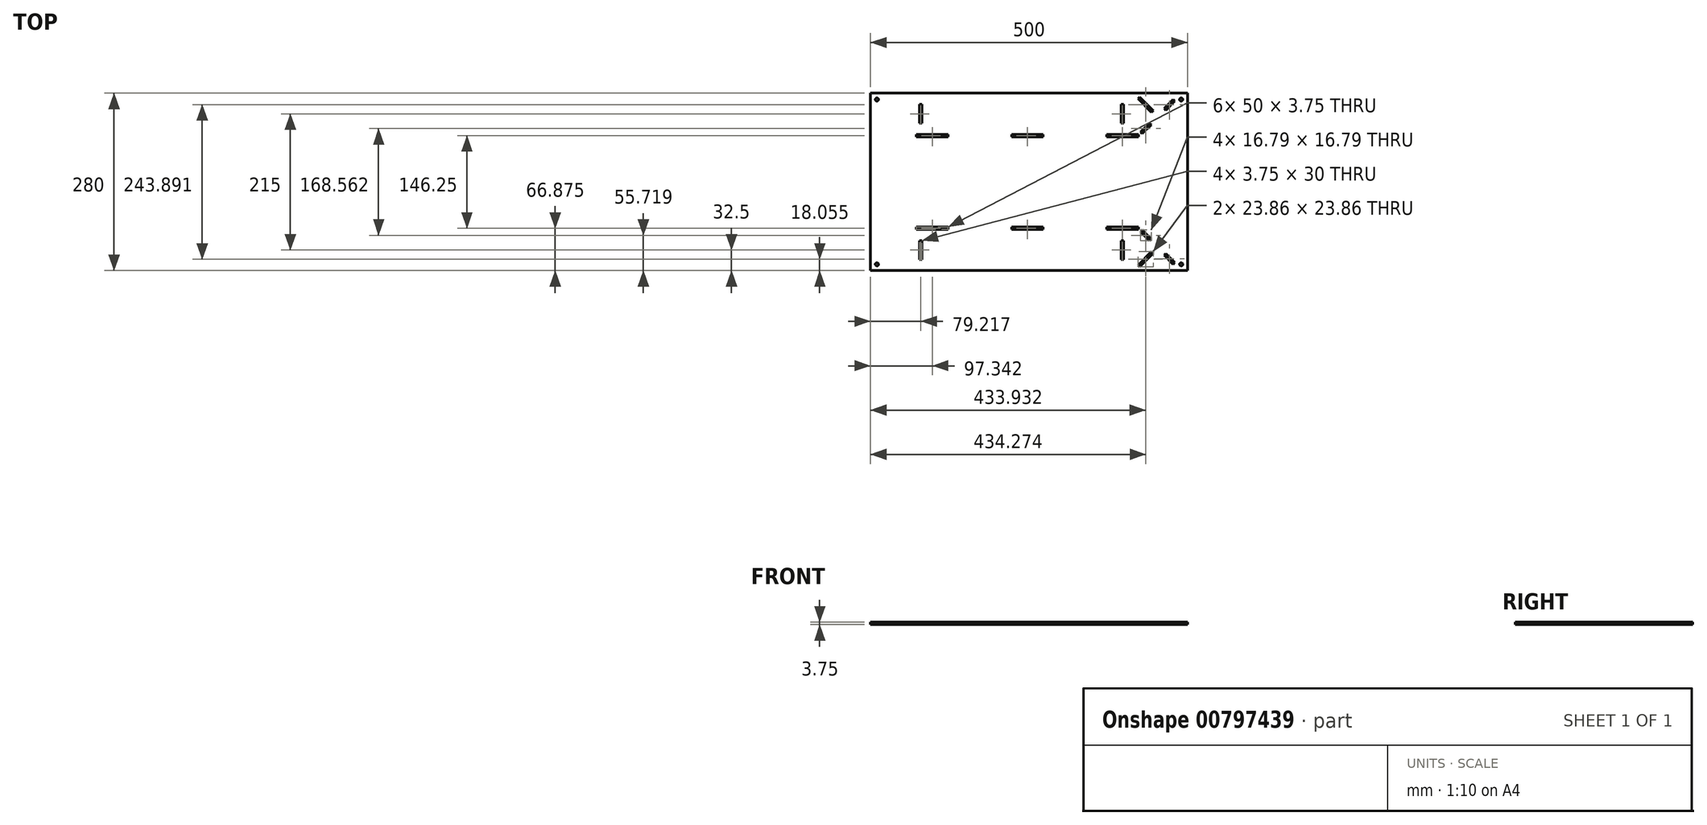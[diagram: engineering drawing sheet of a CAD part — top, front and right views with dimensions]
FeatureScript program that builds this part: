
annotation { "Feature Type Name" : "Feature", "Feature Type Description" : "" }
export const myFeature = defineFeature(function(context is Context, id is Id, definition is map)
    precondition{}
    {
        {
            var Q0;
            Q0=qCreatedBy(makeId("Top.planeOp"),FACE);
            var sketch = newSketch(context, id + "F0", { "sketchPlane" : qUnion([Q0])});
            skLineSegment(sketch, "E0.bottom", {"start": v(12.1, 0) * mm, "end": v(462.1, 0) * mm});
            skLineSegment(sketch, "E0.top", {"start": v(62.1, 280) * mm, "end": v(462.1, 280) * mm});
            skLineSegment(sketch, "E0.right", {"start": v(462.1, 0) * mm, "end": v(462.1, 280) * mm});
            skLineSegment(sketch, "E1.bottom", {"start": v(184.43, 215) * mm, "end": v(234.43, 215) * mm});
            skLineSegment(sketch, "E1.top", {"start": v(184.43, 211.25) * mm, "end": v(234.43, 211.25) * mm});
            skLineSegment(sketch, "E1.left", {"start": v(184.43, 215) * mm, "end": v(184.43, 211.25) * mm});
            skLineSegment(sketch, "E1.right", {"start": v(234.43, 215) * mm, "end": v(234.43, 211.25) * mm});
            skLineSegment(sketch, "E2.MirrorCS", {"start": v(334.43, 215) * mm, "end": v(334.43, 215) * mm});
            skLineSegment(sketch, "E3.MirrorCS", {"start": v(134.43, 65) * mm, "end": v(234.43, 65) * mm});
            skLineSegment(sketch, "E4.MirrorCS", {"start": v(334.43, 65) * mm, "end": v(334.43, 65) * mm});
            skLineSegment(sketch, "E5.bottom", {"start": v(357.56, 262.5) * mm, "end": v(361.3, 262.5) * mm});
            skLineSegment(sketch, "E5.top", {"start": v(357.56, 232.5) * mm, "end": v(361.3, 232.5) * mm});
            skLineSegment(sketch, "E5.left", {"start": v(357.56, 262.5) * mm, "end": v(357.56, 232.5) * mm});
            skLineSegment(sketch, "E5.right", {"start": v(361.3, 262.5) * mm, "end": v(361.3, 232.5) * mm});
            skLineSegment(sketch, "E6.bottom", {"start": v(334.43, 215) * mm, "end": v(384.43, 215) * mm});
            skLineSegment(sketch, "E6.top", {"start": v(334.43, 211.25) * mm, "end": v(384.43, 211.25) * mm});
            skLineSegment(sketch, "E6.left", {"start": v(334.43, 215) * mm, "end": v(334.43, 211.25) * mm});
            skLineSegment(sketch, "E6.right", {"start": v(384.43, 215) * mm, "end": v(384.43, 211.25) * mm});
            skLineSegment(sketch, "E7.bottom", {"start": v(234.43, 65) * mm, "end": v(184.43, 65) * mm});
            skLineSegment(sketch, "E7.top", {"start": v(234.43, 68.75) * mm, "end": v(184.43, 68.75) * mm});
            skLineSegment(sketch, "E7.left", {"start": v(234.43, 65) * mm, "end": v(234.43, 68.75) * mm});
            skLineSegment(sketch, "E7.right", {"start": v(184.43, 65) * mm, "end": v(184.43, 68.75) * mm});
            skLineSegment(sketch, "E8.bottom", {"start": v(334.43, 65) * mm, "end": v(384.43, 65) * mm});
            skLineSegment(sketch, "E8.top", {"start": v(334.43, 68.75) * mm, "end": v(384.43, 68.75) * mm});
            skLineSegment(sketch, "E8.left", {"start": v(334.43, 65) * mm, "end": v(334.43, 68.75) * mm});
            skLineSegment(sketch, "E8.right", {"start": v(384.43, 65) * mm, "end": v(384.43, 68.75) * mm});
            skLineSegment(sketch, "E9.bottom", {"start": v(357.56, 47.5) * mm, "end": v(361.3, 47.5) * mm});
            skLineSegment(sketch, "E9.top", {"start": v(357.56, 17.5) * mm, "end": v(361.3, 17.5) * mm});
            skLineSegment(sketch, "E9.left", {"start": v(357.56, 47.5) * mm, "end": v(357.56, 17.5) * mm});
            skLineSegment(sketch, "E9.right", {"start": v(361.3, 47.5) * mm, "end": v(361.3, 17.5) * mm});
            skLineSegment(sketch, "E10.bottom", {"start": v(62.1, 280) * mm, "end": v(-37.9, 280) * mm});
            skLineSegment(sketch, "E10.top", {"start": v(12.1, 0) * mm, "end": v(-37.9, 0) * mm});
            skLineSegment(sketch, "E10.right", {"start": v(-37.9, 280) * mm, "end": v(-37.9, 0) * mm});
            skLineSegment(sketch, "E11.bottom", {"start": v(84.43, 215) * mm, "end": v(34.43, 215) * mm});
            skLineSegment(sketch, "E11.top", {"start": v(84.43, 211.25) * mm, "end": v(34.43, 211.25) * mm});
            skLineSegment(sketch, "E11.left", {"start": v(84.43, 215) * mm, "end": v(84.43, 211.25) * mm});
            skLineSegment(sketch, "E11.right", {"start": v(34.43, 215) * mm, "end": v(34.43, 211.25) * mm});
            skLineSegment(sketch, "E12.bottom", {"start": v(84.43, 68.75) * mm, "end": v(34.43, 68.75) * mm});
            skLineSegment(sketch, "E12.top", {"start": v(84.43, 65) * mm, "end": v(34.43, 65) * mm});
            skLineSegment(sketch, "E12.left", {"start": v(84.43, 68.75) * mm, "end": v(84.43, 65) * mm});
            skLineSegment(sketch, "E12.right", {"start": v(34.43, 68.75) * mm, "end": v(34.43, 65) * mm});
            skLineSegment(sketch, "E13.bottom", {"start": v(39.43, 262.5) * mm, "end": v(43.18, 262.5) * mm});
            skLineSegment(sketch, "E13.top", {"start": v(39.43, 232.5) * mm, "end": v(43.18, 232.5) * mm});
            skLineSegment(sketch, "E13.left", {"start": v(39.43, 262.5) * mm, "end": v(39.43, 232.5) * mm});
            skLineSegment(sketch, "E13.right", {"start": v(43.18, 262.5) * mm, "end": v(43.18, 232.5) * mm});
            skLineSegment(sketch, "E14.bottom", {"start": v(39.43, 47.5) * mm, "end": v(43.18, 47.5) * mm});
            skLineSegment(sketch, "E14.top", {"start": v(39.43, 17.5) * mm, "end": v(43.18, 17.5) * mm});
            skLineSegment(sketch, "E14.left", {"start": v(39.43, 47.5) * mm, "end": v(39.43, 17.5) * mm});
            skLineSegment(sketch, "E14.right", {"start": v(43.18, 47.5) * mm, "end": v(43.18, 17.5) * mm});
            skSolve(sketch);
        }
        {
            var Q0;
            Q0=makeQuery(id+"F0.imprint","IMPRINT",FACE,{"disambiguationData":[TD([[makeQuery(id+"F0.imprint","IMPRINT",EDGE,{"derivedFrom":sQuery(id+"F0.wireOp",EDGE,"E0.bottom")}),1.0]])]});
            extrude(context, id + "F1", {"entities" : qUnion([Q0]), "depth" : 3.75 * mm, "offsetDistance" : 25 * mm});
        }
        {
            var Q0;
            Q0=makeQuery(id+"F1.opExtrude","CAP_FACE",FACE,{"disambiguationData":[OSD([sQuery(id+"F0.wireOp",EDGE,"E0.bottom"),sQuery(id+"F0.wireOp",EDGE,"E0.top"),sQuery(id+"F0.wireOp",EDGE,"E0.left"),sQuery(id+"F0.wireOp",EDGE,"E0.right"),sQuery(id+"F0.wireOp",EDGE,"E1.bottom"),sQuery(id+"F0.wireOp",EDGE,"E1.top"),sQuery(id+"F0.wireOp",EDGE,"E1.left"),sQuery(id+"F0.wireOp",EDGE,"E1.right"),sQuery(id+"F0.wireOp",EDGE,"e73540e0-437e-4d11-b89e-325f1f7d4c790.MirrorCS"),sQuery(id+"F0.wireOp",EDGE,"E2.MirrorCS"),sQuery(id+"F0.wireOp",EDGE,"06532218-7f8b-4a41-8e3c-2a9fed56a3b10.MirrorCS"),sQuery(id+"F0.wireOp",EDGE,"7cb798fc-15e8-495b-8a35-73028b4edfa90.MirrorCS"),sQuery(id+"F0.wireOp",EDGE,"545d7cc9-1fc7-4841-af53-376eaec099370.MirrorCS"),sQuery(id+"F0.wireOp",EDGE,"E3.MirrorCS"),sQuery(id+"F0.wireOp",EDGE,"9b8ca559-61c4-4ae6-86d6-e5e959e65d2c0.MirrorCS"),sQuery(id+"F0.wireOp",EDGE,"461afd8d-256b-4b3b-8858-7b4be28ac2ee0.MirrorCS"),sQuery(id+"F0.wireOp",EDGE,"ccdc6204-bf97-4cc3-8a27-938706aa7f700.MirrorCS"),sQuery(id+"F0.wireOp",EDGE,"E4.MirrorCS"),sQuery(id+"F0.wireOp",EDGE,"de380e3f-fddb-4eb0-9c14-f8c98a16e2c70.MirrorCS"),sQuery(id+"F0.wireOp",EDGE,"ee423979-f3e1-44e8-98c6-b9dc3032ede40.MirrorCS"),sQuery(id+"F0.wireOp",EDGE,"E5.bottom"),sQuery(id+"F0.wireOp",EDGE,"E5.top"),sQuery(id+"F0.wireOp",EDGE,"E5.left"),sQuery(id+"F0.wireOp",EDGE,"E5.right"),sQuery(id+"F0.wireOp",EDGE,"2a4d6bfd-6cea-46ef-a5a2-565ee4e24cbc0.MirrorCS"),sQuery(id+"F0.wireOp",EDGE,"e7e3dcee-2f9a-4279-8a5c-00eaed48cf630.MirrorCS"),sQuery(id+"F0.wireOp",EDGE,"b1a6a120-30f8-47bb-a578-e070e3f1ff540.MirrorCS"),sQuery(id+"F0.wireOp",EDGE,"80d5920c-4993-49ba-a786-e7242780b6720.MirrorCS")])],"isStart":false});
            var sketch = newSketch(context, id + "F2", { "sketchPlane" : qUnion([Q0])});
            skPoint(sketch, "E15", {"position": v(-27.9, 10) * mm});
            skPoint(sketch, "E16", {"position": v(-27.9, 270) * mm});
            skPoint(sketch, "E17", {"position": v(452.1, 270) * mm});
            skPoint(sketch, "E18", {"position": v(452.1, 10) * mm});
            skSolve(sketch);
        }
        {
            var Q0;
            Q0=sQuery(id+"F2.wireOp",VERTEX,"E15");
            var Q1;
            Q1=sQuery(id+"F2.wireOp",VERTEX,"E16");
            var Q2;
            Q2=sQuery(id+"F2.wireOp",VERTEX,"E18");
            var Q3;
            Q3=sQuery(id+"F2.wireOp",VERTEX,"E17");
            var Q4;
            Q4=makeQuery(id+"F1.opExtrude","SWEPT_BODY",BODY,{"disambiguationData":[OSD([sQuery(id+"F0.wireOp",EDGE,"E0.bottom"),sQuery(id+"F0.wireOp",EDGE,"E0.top"),sQuery(id+"F0.wireOp",EDGE,"E0.left"),sQuery(id+"F0.wireOp",EDGE,"E0.right"),sQuery(id+"F0.wireOp",EDGE,"E1.bottom"),sQuery(id+"F0.wireOp",EDGE,"E1.top"),sQuery(id+"F0.wireOp",EDGE,"E1.left"),sQuery(id+"F0.wireOp",EDGE,"E1.right"),sQuery(id+"F0.wireOp",EDGE,"e73540e0-437e-4d11-b89e-325f1f7d4c790.MirrorCS"),sQuery(id+"F0.wireOp",EDGE,"E2.MirrorCS"),sQuery(id+"F0.wireOp",EDGE,"06532218-7f8b-4a41-8e3c-2a9fed56a3b10.MirrorCS"),sQuery(id+"F0.wireOp",EDGE,"7cb798fc-15e8-495b-8a35-73028b4edfa90.MirrorCS"),sQuery(id+"F0.wireOp",EDGE,"545d7cc9-1fc7-4841-af53-376eaec099370.MirrorCS"),sQuery(id+"F0.wireOp",EDGE,"E3.MirrorCS"),sQuery(id+"F0.wireOp",EDGE,"9b8ca559-61c4-4ae6-86d6-e5e959e65d2c0.MirrorCS"),sQuery(id+"F0.wireOp",EDGE,"461afd8d-256b-4b3b-8858-7b4be28ac2ee0.MirrorCS"),sQuery(id+"F0.wireOp",EDGE,"ccdc6204-bf97-4cc3-8a27-938706aa7f700.MirrorCS"),sQuery(id+"F0.wireOp",EDGE,"E4.MirrorCS"),sQuery(id+"F0.wireOp",EDGE,"de380e3f-fddb-4eb0-9c14-f8c98a16e2c70.MirrorCS"),sQuery(id+"F0.wireOp",EDGE,"ee423979-f3e1-44e8-98c6-b9dc3032ede40.MirrorCS"),sQuery(id+"F0.wireOp",EDGE,"E5.bottom"),sQuery(id+"F0.wireOp",EDGE,"E5.top"),sQuery(id+"F0.wireOp",EDGE,"E5.left"),sQuery(id+"F0.wireOp",EDGE,"E5.right"),sQuery(id+"F0.wireOp",EDGE,"2a4d6bfd-6cea-46ef-a5a2-565ee4e24cbc0.MirrorCS"),sQuery(id+"F0.wireOp",EDGE,"e7e3dcee-2f9a-4279-8a5c-00eaed48cf630.MirrorCS"),sQuery(id+"F0.wireOp",EDGE,"b1a6a120-30f8-47bb-a578-e070e3f1ff540.MirrorCS"),sQuery(id+"F0.wireOp",EDGE,"80d5920c-4993-49ba-a786-e7242780b6720.MirrorCS")])]});
            hole(context, id + "F3", {"style" : HoleStyle.SIMPLE, "endStyle" : HoleEndStyle.THROUGH, "holeDiameter" : 5 * mm, "majorDiameter" : 5 * mm, "isTappedThrough" : true, "tappedDepth" : 12 * mm, "tapClearance" : 3, "locations" : qUnion([Q0, Q1, Q2, Q3]), "scope" : qUnion([Q4])});
        }
        {
            var Q0;
            Q0=makeQuery(id+"F1.opExtrude","CAP_FACE",FACE,{"disambiguationData":[OSD([sQuery(id+"F0.wireOp",EDGE,"E0.bottom"),sQuery(id+"F0.wireOp",EDGE,"E0.top"),sQuery(id+"F0.wireOp",EDGE,"E0.left"),sQuery(id+"F0.wireOp",EDGE,"E0.right"),sQuery(id+"F0.wireOp",EDGE,"E1.bottom"),sQuery(id+"F0.wireOp",EDGE,"E1.top"),sQuery(id+"F0.wireOp",EDGE,"E1.left"),sQuery(id+"F0.wireOp",EDGE,"E1.right"),sQuery(id+"F0.wireOp",EDGE,"E5.bottom"),sQuery(id+"F0.wireOp",EDGE,"E5.top"),sQuery(id+"F0.wireOp",EDGE,"E5.left"),sQuery(id+"F0.wireOp",EDGE,"E5.right"),sQuery(id+"F0.wireOp",EDGE,"E6.bottom"),sQuery(id+"F0.wireOp",EDGE,"E6.top"),sQuery(id+"F0.wireOp",EDGE,"E6.left"),sQuery(id+"F0.wireOp",EDGE,"E6.right"),sQuery(id+"F0.wireOp",EDGE,"E7.bottom"),sQuery(id+"F0.wireOp",EDGE,"E7.top"),sQuery(id+"F0.wireOp",EDGE,"E7.left"),sQuery(id+"F0.wireOp",EDGE,"E7.right"),sQuery(id+"F0.wireOp",EDGE,"E8.bottom"),sQuery(id+"F0.wireOp",EDGE,"E8.top"),sQuery(id+"F0.wireOp",EDGE,"E8.left"),sQuery(id+"F0.wireOp",EDGE,"E8.right"),sQuery(id+"F0.wireOp",EDGE,"E9.bottom"),sQuery(id+"F0.wireOp",EDGE,"E9.top"),sQuery(id+"F0.wireOp",EDGE,"E9.left"),sQuery(id+"F0.wireOp",EDGE,"E9.right")])],"isStart":false});
            var sketch = newSketch(context, id + "F4", { "sketchPlane" : qUnion([Q0])});
            skLineSegment(sketch, "E19", {"start": v(384.43, 215) * mm, "end": v(402.1, 232.68) * mm});
            skLineSegment(sketch, "E20", {"start": v(439.43, 270) * mm, "end": v(442.08, 267.35) * mm});
            skLineSegment(sketch, "E21", {"start": v(442.08, 267.35) * mm, "end": v(427.94, 253.2) * mm});
            skLineSegment(sketch, "E22", {"start": v(390.62, 215.88) * mm, "end": v(387.97, 218.54) * mm});
            skLineSegment(sketch, "E23", {"start": v(402.1, 232.68) * mm, "end": v(404.76, 230.03) * mm});
            skLineSegment(sketch, "E24", {"start": v(425.29, 255.86) * mm, "end": v(427.94, 253.2) * mm});
            skLineSegment(sketch, "E25.trimOffspring", {"start": v(425.29, 255.86) * mm, "end": v(439.43, 270) * mm});
            skLineSegment(sketch, "E26.trimOffspring", {"start": v(404.76, 230.03) * mm, "end": v(390.62, 215.88) * mm});
            skPoint(sketch, "E27", {"position": v(413.7, 244.27) * mm});
            skLineSegment(sketch, "E28", {"start": v(384.09, 271.23) * mm, "end": v(384.09, 271.23) * mm});
            skLineSegment(sketch, "E29", {"start": v(384.09, 271.23) * mm, "end": v(405.3, 250.01) * mm});
            skLineSegment(sketch, "E30", {"start": v(407.95, 252.66) * mm, "end": v(405.3, 250.01) * mm});
            skLineSegment(sketch, "E31", {"start": v(407.95, 252.66) * mm, "end": v(386.74, 273.88) * mm});
            skLineSegment(sketch, "E32", {"start": v(384.09, 271.23) * mm, "end": v(386.74, 273.88) * mm});
            skLineSegment(sketch, "E33", {"start": v(462.1, 140) * mm, "end": v(-37.9, 140) * mm});
            skLineSegment(sketch, "E34.MirrorCS", {"start": v(384.09, 8.77) * mm, "end": v(386.74, 6.12) * mm});
            skLineSegment(sketch, "E35.MirrorCS", {"start": v(407.95, 27.34) * mm, "end": v(405.3, 29.99) * mm});
            skLineSegment(sketch, "E36.MirrorCS", {"start": v(425.29, 24.14) * mm, "end": v(427.94, 26.8) * mm});
            skLineSegment(sketch, "E37.MirrorCS", {"start": v(402.1, 47.32) * mm, "end": v(404.76, 49.97) * mm});
            skLineSegment(sketch, "E38.MirrorCS", {"start": v(439.43, 10) * mm, "end": v(442.08, 12.65) * mm});
            skLineSegment(sketch, "E39.MirrorCS", {"start": v(390.62, 64.12) * mm, "end": v(387.97, 61.46) * mm});
            skPoint(sketch, "E40.MirrorP", {"position": v(413.7, 35.73) * mm});
            skLineSegment(sketch, "E41.MirrorCS", {"start": v(407.95, 27.34) * mm, "end": v(386.74, 6.12) * mm});
            skLineSegment(sketch, "E42.MirrorCS", {"start": v(384.09, 8.77) * mm, "end": v(405.3, 29.99) * mm});
            skLineSegment(sketch, "E43.MirrorCS", {"start": v(404.76, 49.97) * mm, "end": v(390.62, 64.12) * mm});
            skLineSegment(sketch, "E44.MirrorCS", {"start": v(425.29, 24.14) * mm, "end": v(439.43, 10) * mm});
            skLineSegment(sketch, "E45.MirrorCS", {"start": v(384.43, 65) * mm, "end": v(402.1, 47.32) * mm});
            skLineSegment(sketch, "E46.MirrorCS", {"start": v(442.08, 12.65) * mm, "end": v(427.94, 26.8) * mm});
            skSolve(sketch);
        }
        {
            var Q0;
            Q0=makeQuery(id+"F4.imprint","IMPRINT",FACE,{"disambiguationData":[TD([[makeQuery(id+"F4.imprint","IMPRINT",EDGE,{"derivedFrom":sQuery(id+"F4.wireOp",EDGE,"E28")}),-1.0]])]});
            var Q1;
            Q1=makeQuery(id+"F4.imprint","IMPRINT",FACE,{"disambiguationData":[TD([[makeQuery(id+"F4.imprint","IMPRINT",EDGE,{"derivedFrom":sQuery(id+"F4.wireOp",EDGE,"E20")}),-1.0]])]});
            var Q2;
            {var subQ2=sQuery(id+"F4.wireOp",EDGE,"E22");Q2=makeQuery(id+"F4.imprint","IMPRINT",FACE,{"disambiguationData":[TD([[makeQuery(id+"F4.imprint","IMPRINT",EDGE,{"derivedFrom":subQ2}),-1.0]])]});}
            var Q3;
            {var subQ0=sQuery(id+"F4.wireOp",EDGE,"a934c7fb-54da-4184-a665-6b071d04c7bb2.MirrorCS");Q3=makeQuery(id+"F4.imprint","IMPRINT",FACE,{"disambiguationData":[TD([[makeQuery(id+"F4.imprint","IMPRINT",EDGE,{"derivedFrom":subQ0}),1.0]])]});}
            var Q4;
            Q4=makeQuery(id+"F4.imprint","IMPRINT",FACE,{"disambiguationData":[TD([[makeQuery(id+"F4.imprint","IMPRINT",EDGE,{"derivedFrom":sQuery(id+"F4.wireOp",EDGE,"a934c7fb-54da-4184-a665-6b071d04c7bb0.MirrorCS")}),1.0]])]});
            var Q5;
            Q5=makeQuery(id+"F4.imprint","IMPRINT",FACE,{"disambiguationData":[TD([[makeQuery(id+"F4.imprint","IMPRINT",EDGE,{"derivedFrom":sQuery(id+"F4.wireOp",EDGE,"a934c7fb-54da-4184-a665-6b071d04c7bb1.MirrorCS")}),1.0]])]});
            var Q6;
            Q6=makeQuery(id+"F4.imprint","IMPRINT",FACE,{"disambiguationData":[TD([[makeQuery(id+"F4.imprint","IMPRINT",EDGE,{"derivedFrom":sQuery(id+"F4.wireOp",EDGE,"E29")}),1.0]])]});
            var Q7;
            {var subQ0=sQuery(id+"F4.wireOp",EDGE,"E37.MirrorCS");Q7=makeQuery(id+"F4.imprint","IMPRINT",FACE,{"disambiguationData":[TD([[makeQuery(id+"F4.imprint","IMPRINT",EDGE,{"derivedFrom":subQ0}),1.0]])]});}
            var Q8;
            Q8=makeQuery(id+"F4.imprint","IMPRINT",FACE,{"disambiguationData":[TD([[makeQuery(id+"F4.imprint","IMPRINT",EDGE,{"derivedFrom":sQuery(id+"F4.wireOp",EDGE,"E34.MirrorCS")}),1.0]])]});
            var Q9;
            Q9=makeQuery(id+"F4.imprint","IMPRINT",FACE,{"disambiguationData":[TD([[makeQuery(id+"F4.imprint","IMPRINT",EDGE,{"derivedFrom":sQuery(id+"F4.wireOp",EDGE,"E36.MirrorCS")}),-1.0]])]});
            extrude(context, id + "F5", {"entities" : qUnion([Q0, Q1, Q2, Q3, Q4, Q5, Q6, Q7, Q8, Q9]), "operationType" : NewBodyOperationType.REMOVE, "oppositeDirection" : true, "depth" : 3.75 * mm, "offsetDistance" : 25 * mm});
        }
    });
